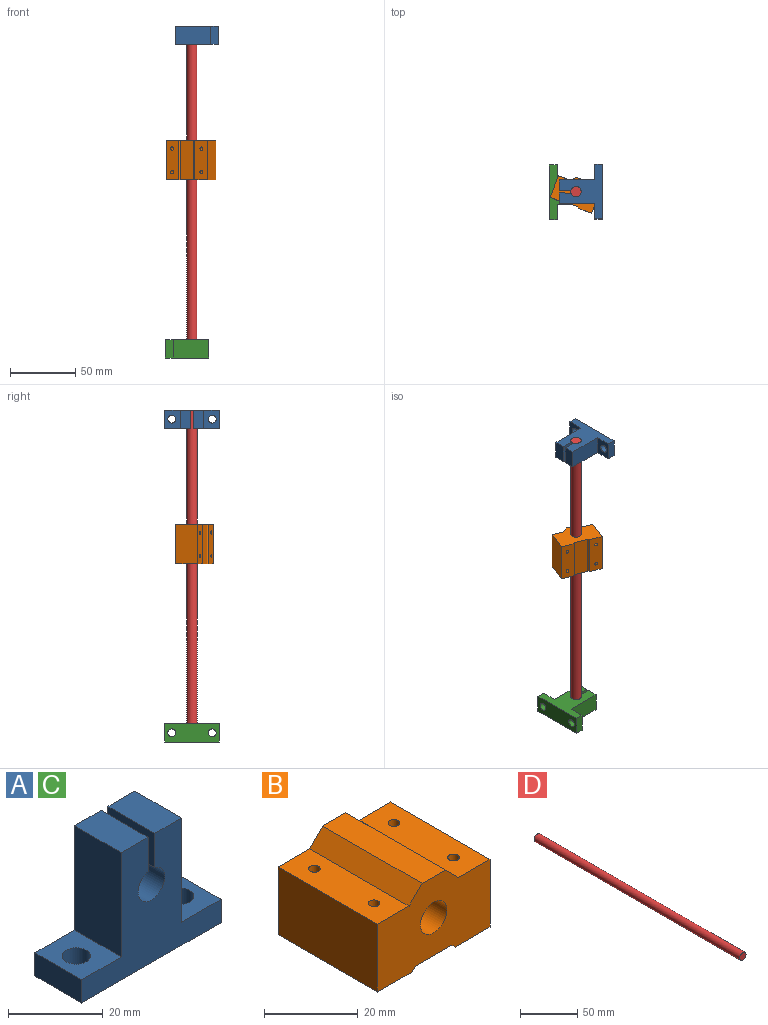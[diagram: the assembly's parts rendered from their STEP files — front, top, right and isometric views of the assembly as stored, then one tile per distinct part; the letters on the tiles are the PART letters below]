
ASSEMBLY  parts=4 mates=4
PART A: 16 faces, bbox 41.7x14x33 mm
  f0: plane 14x8mm, normal (0,0,1), area 112mm2, adj f2,f4,f11,f15
  f1: cylinder r=4mm len=14mm, axis (0,1,0), area 323.6mm2, adj f2,f11,f14,f15
  f2: plane 41.7x33mm, normal (0,-1,0), area 668.5mm2, adj f0,f1,f3,f4,f5,f6,f7,f8
  f3: plane 14x8mm, normal (0,0,1), area 112mm2, adj f2,f10,f11,f14
  f4: plane 27x14mm, normal (-1,0,0), area 378mm2, adj f0,f2,f5,f11
  f5: plane 14x11.85mm, normal (0,0,1), area 137.6mm2, adj f2,f4,f6,f11,f12
  f6: plane 14x6mm, normal (-1,0,0), area 84mm2, adj f2,f5,f7,f11
  f7: plane 41.7x14mm, normal (0,0,-1), area 527.3mm2, adj f2,f6,f8,f11,f12,f13
  f8: plane 14x6mm, normal (1,0,0), area 84mm2, adj f2,f7,f9,f11
  f9: plane 14x11.85mm, normal (0,0,1), area 137.6mm2, adj f2,f8,f10,f11,f13
  f10: plane 27x14mm, normal (1,0,0), area 378mm2, adj f2,f3,f9,f11
  f11: plane 41.7x33mm, normal (0,1,0), area 668.5mm2, adj f0,f1,f3,f4,f5,f6,f7,f8
  f12: cylinder r=3mm len=6mm, axis (0,0,1), area 113.1mm2, adj f5,f7
  f13: cylinder r=3mm len=6mm, axis (0,0,1), area 113.1mm2, adj f7,f9
  f14: plane 14x8.83mm, normal (-1,0,0), area 123.6mm2, adj f1,f2,f3,f11
  f15: plane 14x8.83mm, normal (1,0,0), area 123.6mm2, adj f0,f1,f2,f11
PART B: 19 faces, bbox 34x30x21.7 mm
  f0: plane 30x10.5mm, normal (0,0,-1), area 305.2mm2, adj f1,f7,f11,f13,f14,f16
  f1: plane 34x21.65mm, normal (0,1,0), area 582.8mm2, adj f0,f2,f3,f4,f5,f6,f7,f8
  f2: plane 30x7mm, normal (0,0,1), area 210mm2, adj f1,f3,f10,f11
  f3: plane 30x3.95mm, normal (-0.71,0,0.71), area 167.6mm2, adj f1,f2,f4,f11
  f4: plane 30x9.55mm, normal (0,0,1), area 276.7mm2, adj f1,f3,f5,f11,f12,f15
  f5: plane 30x17.7mm, normal (-1,0,0), area 531mm2, adj f1,f4,f6,f11
  f6: plane 30x10.5mm, normal (0,0,-1), area 305.2mm2, adj f1,f5,f11,f12,f15,f18
  f7: plane 30x17.7mm, normal (1,0,0), area 531mm2, adj f0,f1,f8,f11
  f8: plane 30x9.55mm, normal (0,0,1), area 276.7mm2, adj f1,f7,f10,f11,f13,f14
  f9: cylinder r=4mm len=30mm, axis (0,1,0), area 754mm2, adj f1,f11
  f10: plane 30x3.95mm, normal (0.71,0,0.71), area 167.6mm2, adj f1,f2,f8,f11
  f11: plane 34x21.65mm, normal (0,-1,0), area 582.8mm2, adj f0,f2,f3,f4,f5,f6,f7,f8
  f12: cylinder r=1.25mm len=17.7mm, axis (0,0,-1), area 139mm2, adj f4,f6
  f13: cylinder r=1.25mm len=17.7mm, axis (0,0,-1), area 139mm2, adj f0,f8
  f14: cylinder r=1.25mm len=17.7mm, axis (0,0,-1), area 139mm2, adj f0,f8
  f15: cylinder r=1.25mm len=17.7mm, axis (0,0,-1), area 139mm2, adj f4,f6
  f16: plane 30x1mm, normal (-0.71,0,-0.71), area 42.4mm2, adj f0,f1,f11,f17
  f17: plane 30x11mm, normal (0,0,-1), area 330mm2, adj f1,f11,f16,f18
  f18: plane 30x1mm, normal (0.71,0,-0.71), area 42.4mm2, adj f1,f6,f11,f17
PART C: same geometry as A
PART D: 3 faces, bbox 8x254x8 mm
  f0: cylinder r=4mm len=254mm, axis (0,1,0), area 6383.7mm2, adj f1,f2
  f1: plane 8x8mm, normal (0,-1,0), area 50.3mm2, adj f0
  f2: plane 8x8mm, normal (0,1,0), area 50.3mm2, adj f0
PLACE A rot(axis=(0.58,-0.58,-0.58),120deg) t=(27.57,-0.02,247)mm
PLACE B rot(axis=(0.13,0.7,0.7),165.1deg) t=(7.27,0,151.24)mm
PLACE C rot(axis=(0.58,0.58,0.58),120deg) t=(-13.03,0,7)mm
PLACE D rot(axis=(0.58,0.58,0.58),120deg) t=(7.27,0,254)mm
MATE fastened C.f1 <-> D.f0  axis (0,0,-1) through (7.27,0,0)mm
MATE planar A.f11 <-> D.f0  axis (0,0,1) through (14.55,-0.01,254)mm
MATE cylindrical A.f1 <-> D.f0  axis (0,0,1) through (7.27,0,254)mm
MATE cylindrical B.f9 <-> D.f0  axis (0,0,1) through (7.27,0,151.24)mm
